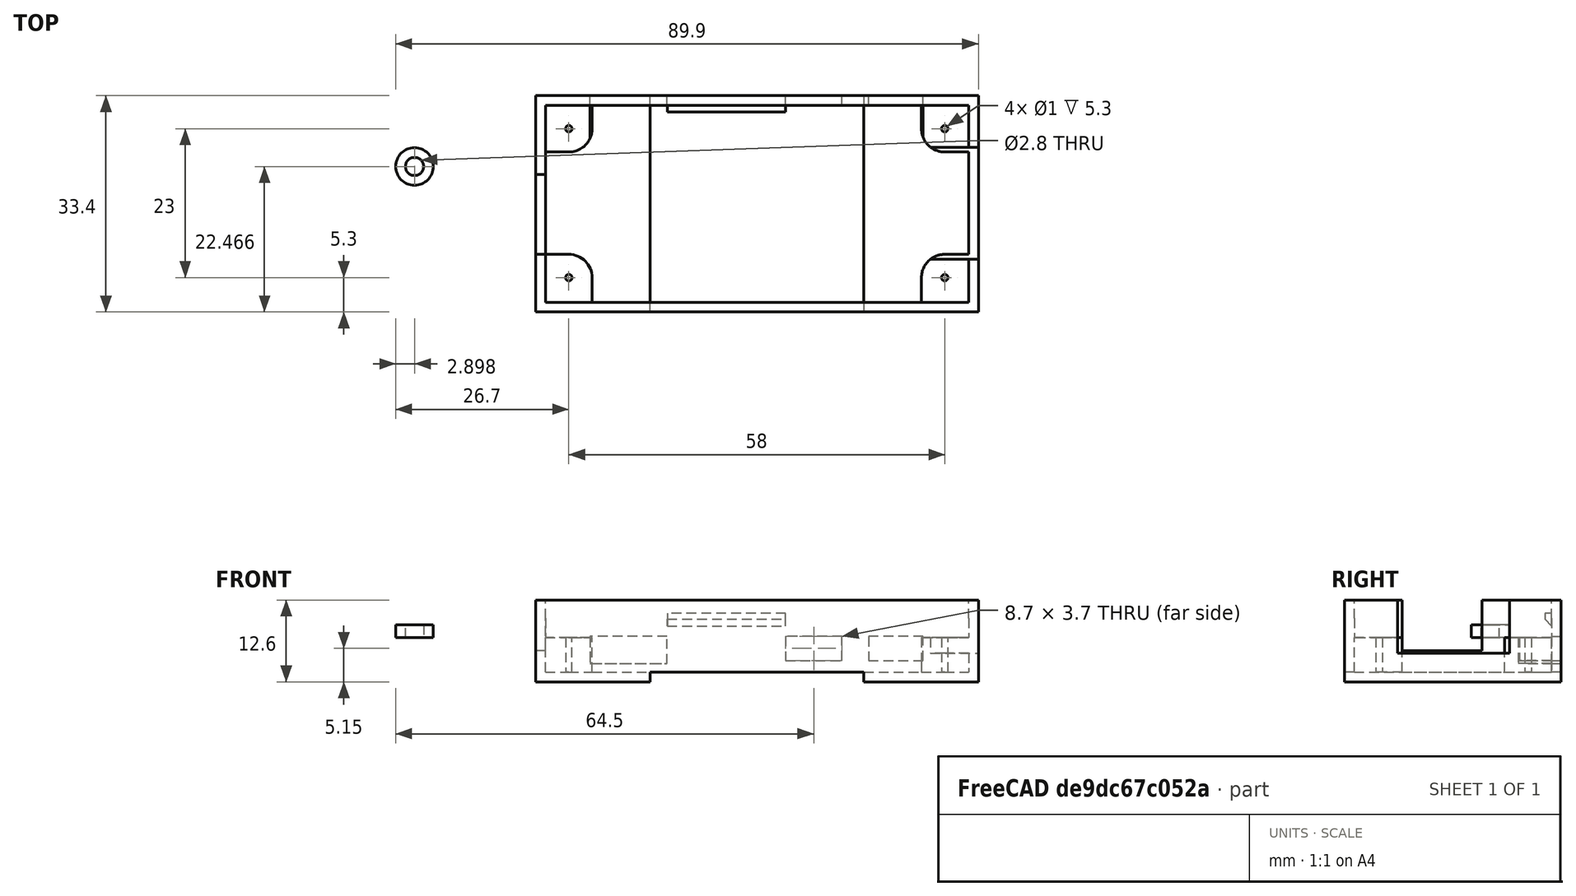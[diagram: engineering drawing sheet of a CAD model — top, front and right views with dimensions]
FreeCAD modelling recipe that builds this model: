
FCSTD DOCUMENT  (FreeCAD 0.18.3R)
Label: PI.Capsule
License: All rights reserved
LicenseURL: http://en.wikipedia.org/wiki/All_rights_reserved
objects: Part::Part2DObjectPython×32, Part::Extrusion×32, Part::Cut×15, Part::MultiFuse×7
note: 86 computed .brp shape members not serialized (recipe doc carries the construction recipe); baked Part::Feature solids carry a one-line shape summary decoded from their .brp

FEATURE [Part::Part2DObjectPython] Rectangle  # Draft 2D object (typed FeaturePython)
  ChamferSize = 0
  Columns = 1
  FilletRadius = 0
  Height = 33.4
  Length = 68.3
  MakeFace = true
  Placement = pos=(0,0,0) rot=(1,0,0;3.14159rad)
  Rows = 1
FEATURE [Part::Part2DObjectPython] Rectangle001  # Draft 2D object (typed FeaturePython)
  ChamferSize = 0
  Columns = 1
  FilletRadius = 0
  Height = 30.4
  Length = 65.3
  MakeFace = true
  Placement = pos=(1.5,-1.5,0) rot=(1,0,0;3.14159rad)
  Rows = 1
FEATURE [Part::Part2DObjectPython] Circle004  # Draft 2D object (typed FeaturePython)
  FirstAngle = 0
  LastAngle = 0
  MakeFace = true
  Placement = pos=(5.1,-5.1,-8.3) rot=(0,0,-1;1.5708rad)
  Radius = 3.6
FEATURE [Part::Part2DObjectPython] Circle006  # Draft 2D object (typed FeaturePython)
  FirstAngle = 0
  LastAngle = 0
  MakeFace = true
  Placement = pos=(63.1,-5.1,-8.3) rot=(0,0,1;0rad)
  Radius = 3.6
FEATURE [Part::Part2DObjectPython] Rectangle006  # Draft 2D object (typed FeaturePython)
  ChamferSize = 0
  Columns = 1
  FilletRadius = 0
  Height = 4.1
  Length = 11.9
  MakeFace = true
  Placement = pos=(8.375,-1.5,-7) rot=(1,0,0;1.5708rad)
  Rows = 1
FEATURE [Part::Part2DObjectPython] Rectangle007  # Draft 2D object (typed FeaturePython)
  ChamferSize = 0
  Columns = 1
  FilletRadius = 0
  Height = 3.7
  Length = 8.7
  MakeFace = true
  Placement = pos=(38.55,-1.5,-6.5) rot=(1,0,0;1.5708rad)
  Rows = 1
FEATURE [Part::Part2DObjectPython] Rectangle008  # Draft 2D object (typed FeaturePython)
  ChamferSize = 0
  Columns = 1
  FilletRadius = 0
  Height = 3.7
  Length = 8.4
  MakeFace = true
  Placement = pos=(51.35,-1.5,-6.5) rot=(1,0,0;1.5708rad)
  Rows = 1
  Support = -> [Rectangle007]
FEATURE [Part::Extrusion] Extrude020
  Base = -> Circle006
  Dir = (0,0,1)
  DirMode = 2
  FaceMakerClass = Part::FaceMakerBullseye
  LengthFwd = 5.3
  LengthRev = 0
  Solid = false
  Symmetric = false
FEATURE [Part::Extrusion] Extrude021
  Base = -> Circle004
  Dir = (0,0,1)
  DirMode = 2
  FaceMakerClass = Part::FaceMakerBullseye
  LengthFwd = 5.3
  LengthRev = 0
  Solid = false
  Symmetric = false
FEATURE [Part::Part2DObjectPython] Rectangle013  # Draft 2D object (typed FeaturePython)
  ChamferSize = 0
  Columns = 1
  FilletRadius = 0
  Height = 7.2
  Length = 3.6
  MakeFace = true
  Placement = pos=(1.5,-8.7,-8.3) rot=(0,0,1;0rad)
  Rows = 1
  Support = -> [Rectangle]
FEATURE [Part::Part2DObjectPython] Rectangle014  # Draft 2D object (typed FeaturePython)
  ChamferSize = 0
  Columns = 1
  FilletRadius = 0
  Height = 3.6
  Length = 7.2
  MakeFace = true
  Placement = pos=(1.5,-5.1,-8.3) rot=(0,0,1;0rad)
  Rows = 1
FEATURE [Part::Part2DObjectPython] Circle008  # Draft 2D object (typed FeaturePython)
  FirstAngle = 0
  LastAngle = 0
  MakeFace = true
  Placement = pos=(63.1,-5.1,-8.3) rot=(0,0,1;0rad)
  Radius = 0.5
FEATURE [Part::Extrusion] Extrude027
  Base = -> Circle008
  Dir = (0,0,1)
  DirMode = 2
  FaceMakerClass = Part::FaceMakerBullseye
  LengthFwd = 5.3
  LengthRev = 0
  Solid = false
  Symmetric = false
FEATURE [Part::Extrusion] Extrude028
  Base = -> Rectangle013
  Dir = (0,0,1)
  DirMode = 2
  FaceMakerClass = Part::FaceMakerBullseye
  LengthFwd = 5.3
  LengthRev = 0
  Solid = false
  Symmetric = false
FEATURE [Part::Extrusion] Extrude029
  Base = -> Rectangle014
  Dir = (0,0,1)
  DirMode = 2
  FaceMakerClass = Part::FaceMakerBullseye
  LengthFwd = 5.3
  LengthRev = 0
  Solid = false
  Symmetric = false
FEATURE [Part::MultiFuse] Fusion002
  Shapes = -> [Extrude028,Extrude029,Extrude021]
FEATURE [Part::Part2DObjectPython] Circle009  # Draft 2D object (typed FeaturePython)
  FirstAngle = 0
  LastAngle = 0
  MakeFace = true
  Placement = pos=(5.1,-5.1,-8.3) rot=(0,0,1;0rad)
  Radius = 0.5
FEATURE [Part::Extrusion] Extrude030
  Base = -> Circle009
  Dir = (0,0,1)
  DirMode = 2
  FaceMakerClass = Part::FaceMakerBullseye
  LengthFwd = 5.3
  LengthRev = 0
  Solid = false
  Symmetric = false
FEATURE [Part::Cut] Cut002
  Base = -> Fusion002
  Tool = -> Extrude030
FEATURE [Part::Part2DObjectPython] Circle010  # Draft 2D object (typed FeaturePython)
  FirstAngle = 0
  LastAngle = 0
  MakeFace = true
  Placement = pos=(5.1,-28.1,-8.3) rot=(1,0,0;3.14159rad)
  Radius = 0.5
FEATURE [Part::Extrusion] Extrude033
  Base = -> Circle010
  Dir = (0,0,-1)
  DirMode = 2
  FaceMakerClass = Part::FaceMakerBullseye
  LengthFwd = -5.3
  LengthRev = 0
  Solid = false
  Symmetric = false
FEATURE [Part::Part2DObjectPython] Circle011  # Draft 2D object (typed FeaturePython)
  FirstAngle = 0
  LastAngle = 0
  MakeFace = true
  Placement = pos=(5.1,-28.1,-8.3) rot=(1,0,0;3.14159rad)
  Radius = 3.6
FEATURE [Part::Part2DObjectPython] Rectangle019  # Draft 2D object (typed FeaturePython)
  ChamferSize = 0
  Columns = 1
  FilletRadius = 0
  Height = 3.8
  Length = 7.2
  MakeFace = true
  Placement = pos=(1.5,-31.9,-8.3) rot=(0,0,1;0rad)
  Rows = 1
FEATURE [Part::Part2DObjectPython] Rectangle020  # Draft 2D object (typed FeaturePython)
  ChamferSize = 0
  Columns = 1
  FilletRadius = 0
  Height = 7.4
  Length = 3.6
  MakeFace = true
  Placement = pos=(1.5,-31.9,-8.3) rot=(0,0,1;0rad)
  Rows = 1
FEATURE [Part::Extrusion] Extrude
  Base = -> Circle011
  Dir = (0,0,-1)
  DirMode = 2
  FaceMakerClass = Part::FaceMakerBullseye
  LengthFwd = -5.3
  LengthRev = 0
  Solid = false
  Symmetric = false
FEATURE [Part::Extrusion] Extrude034
  Base = -> Rectangle019
  Dir = (0,0,1)
  DirMode = 2
  FaceMakerClass = Part::FaceMakerBullseye
  LengthFwd = 5.3
  LengthRev = 0
  Solid = false
  Symmetric = false
FEATURE [Part::Extrusion] Extrude035
  Base = -> Rectangle020
  Dir = (0,0,1)
  DirMode = 2
  FaceMakerClass = Part::FaceMakerBullseye
  LengthFwd = 5.3
  LengthRev = 0
  Solid = false
  Symmetric = false
FEATURE [Part::MultiFuse] Fusion003
  Shapes = -> [Extrude034,Extrude035,Extrude]
FEATURE [Part::Cut] Cut003
  Base = -> Fusion003
  Tool = -> Extrude033
FEATURE [Part::Extrusion] Extrude036
  Base = -> Rectangle001
  Dir = (0,0,-1)
  DirMode = 2
  FaceMakerClass = Part::FaceMakerBullseye
  LengthFwd = 8.3
  LengthRev = 0
  Solid = false
  Symmetric = false
FEATURE [Part::Extrusion] Extrude037
  Base = -> Rectangle
  Dir = (0,0,-1)
  DirMode = 2
  FaceMakerClass = Part::FaceMakerBullseye
  LengthFwd = 9.8
  LengthRev = 0
  Solid = false
  Symmetric = false
FEATURE [Part::Part2DObjectPython] Circle012  # Draft 2D object (typed FeaturePython)
  FirstAngle = 0
  LastAngle = 0
  MakeFace = true
  Placement = pos=(63.1,-28.1,-3) rot=(0,0,1;0rad)
  Radius = 3.6
FEATURE [Part::Part2DObjectPython] Circle013  # Draft 2D object (typed FeaturePython)
  FirstAngle = 0
  LastAngle = 0
  MakeFace = true
  Placement = pos=(63.1,-28.1,-3) rot=(0,0,1;0rad)
  Radius = 0.5
FEATURE [Part::Part2DObjectPython] Rectangle021  # Draft 2D object (typed FeaturePython)
  ChamferSize = 0
  Columns = 1
  FilletRadius = 0
  Height = 7.4
  Length = 3.7
  MakeFace = true
  Placement = pos=(63.1,-31.9,-3) rot=(0,0,1;0rad)
  Rows = 1
FEATURE [Part::Part2DObjectPython] Rectangle022  # Draft 2D object (typed FeaturePython)
  ChamferSize = 0
  Columns = 1
  FilletRadius = 0
  Height = 3.8
  Length = 7.3
  MakeFace = true
  Placement = pos=(59.5,-31.9,-3) rot=(0,0,1;0rad)
  Rows = 1
FEATURE [Part::Extrusion] Extrude038
  Base = -> Rectangle021
  Dir = (0,0,1)
  DirMode = 2
  FaceMakerClass = Part::FaceMakerBullseye
  LengthFwd = -5.3
  LengthRev = 0
  Solid = false
  Symmetric = false
FEATURE [Part::Extrusion] Extrude039
  Base = -> Rectangle022
  Dir = (0,0,1)
  DirMode = 2
  FaceMakerClass = Part::FaceMakerBullseye
  LengthFwd = -5.3
  LengthRev = 0
  Solid = false
  Symmetric = false
FEATURE [Part::Extrusion] Extrude040
  Base = -> Circle012
  Dir = (0,0,1)
  DirMode = 2
  FaceMakerClass = Part::FaceMakerBullseye
  LengthFwd = -5.3
  LengthRev = 0
  Solid = false
  Symmetric = false
FEATURE [Part::MultiFuse] Fusion
  Shapes = -> [Extrude038,Extrude039,Extrude040]
FEATURE [Part::Extrusion] Extrude041
  Base = -> Circle013
  Dir = (0,0,1)
  DirMode = 2
  FaceMakerClass = Part::FaceMakerBullseye
  LengthFwd = -5.3
  LengthRev = 0
  Solid = false
  Symmetric = false
FEATURE [Part::Cut] Cut
  Base = -> Fusion
  Tool = -> Extrude041
FEATURE [Part::Part2DObjectPython] Rectangle024  # Draft 2D object (typed FeaturePython)
  ChamferSize = 0
  Columns = 1
  FilletRadius = 0
  Height = 3.6
  Length = 7.3
  MakeFace = true
  Placement = pos=(59.5,-5.1,-3) rot=(0,0,1;0rad)
  Rows = 1
FEATURE [Part::Part2DObjectPython] Rectangle025  # Draft 2D object (typed FeaturePython)
  ChamferSize = 0
  Columns = 1
  FilletRadius = 0
  Height = 7.19976
  Length = 3.7019
  MakeFace = true
  Placement = pos=(63.1,-8.7,-3) rot=(0,0,1;0rad)
  Rows = 1
FEATURE [Part::Extrusion] Extrude042
  Base = -> Rectangle025
  Dir = (0,0,1)
  DirMode = 2
  FaceMakerClass = Part::FaceMakerBullseye
  LengthFwd = -5.3
  LengthRev = 0
  Solid = false
  Symmetric = false
FEATURE [Part::Extrusion] Extrude043
  Base = -> Rectangle024
  Dir = (0,0,1)
  DirMode = 2
  FaceMakerClass = Part::FaceMakerBullseye
  LengthFwd = -5.3
  LengthRev = 0
  Solid = false
  Symmetric = false
FEATURE [Part::MultiFuse] Fusion004
  Shapes = -> [Extrude043,Extrude042,Extrude020]
FEATURE [Part::Cut] Cut005
  Base = -> Fusion004
  Tool = -> Extrude027
FEATURE [Part::MultiFuse] Fusion013
  Shapes = -> [Cut005,Cut]
FEATURE [Part::Extrusion] Extrude046
  Base = -> Rectangle006
  Dir = (0,-1,2e-16)
  DirMode = 2
  FaceMakerClass = Part::FaceMakerBullseye
  LengthFwd = 7
  LengthRev = 0
  Solid = false
  Symmetric = false
FEATURE [Part::Cut] Cut008
  Base = -> Cut002
  Tool = -> Extrude046
FEATURE [Part::Part2DObjectPython] Rectangle028  # Draft 2D object (typed FeaturePython)
  ChamferSize = 0
  Columns = 1
  FilletRadius = 0
  Height = 4.2
  Length = 11.9
  MakeFace = true
  Placement = pos=(8.375,-1.5,-7) rot=(1,0,0;1.5708rad)
  Rows = 1
FEATURE [Part::Part2DObjectPython] Rectangle029  # Draft 2D object (typed FeaturePython)
  ChamferSize = 0
  Columns = 1
  FilletRadius = 0
  Height = 3.6
  Length = 8.4
  MakeFace = true
  Placement = pos=(51.35,-1.5,-6.5) rot=(1,0,0;1.5708rad)
  Rows = 1
FEATURE [Part::Extrusion] Extrude050
  Base = -> Rectangle029
  Dir = (0,-1,2e-16)
  DirMode = 2
  FaceMakerClass = Part::FaceMakerBullseye
  LengthFwd = 7
  LengthRev = 0
  Placement = pos=(7.1e-15,-9e-16,0) rot=(0,0,1;0rad)
  Solid = false
  Symmetric = false
FEATURE [Part::Part2DObjectPython] Rectangle048  # Draft 2D object (typed FeaturePython)
  ChamferSize = 0
  Columns = 1
  FilletRadius = 0
  Height = 4.99807
  Length = 12.3
  MakeFace = true
  Placement = pos=(1.5,-24.5,-4.99807) rot=(0.57735,0.57735,0.57735;2.0944rad)
  Rows = 1
FEATURE [Part::Extrusion] Extrude096
  Base = -> Rectangle048
  Dir = (1,0,0)
  DirMode = 2
  FaceMakerClass = Part::FaceMakerBullseye
  LengthFwd = -1.5
  LengthRev = 0
  Solid = false
  Symmetric = false
FEATURE [Part::Part2DObjectPython] Rectangle071  # Draft 2D object (typed FeaturePython)
  ChamferSize = 0
  Columns = 1
  FilletRadius = 0
  Height = 33.4
  Length = 32.95
  MakeFace = true
  Placement = pos=(17.675,2e-15,-9.8) rot=(1,0,0;3.14159rad)
  Rows = 1
FEATURE [Part::Extrusion] Extrude168
  Base = -> Rectangle071
  Dir = (0,0,-1)
  DirMode = 2
  FaceMakerClass = Part::FaceMakerBullseye
  LengthFwd = -1.5
  LengthRev = 0
  Solid = false
  Symmetric = false
FEATURE [Part::Cut] Cut004
  Base = -> Extrude037
  Tool = -> Extrude036
FEATURE [Part::Part2DObjectPython] Rectangle027  # Draft 2D object (typed FeaturePython)
  ChamferSize = 0
  Columns = 1
  FilletRadius = 0
  Height = 5.4
  Length = 17.3
  MakeFace = true
  Placement = pos=(60.9006,-7.95,-5.4) rot=(0.57735,-0.57735,-0.57735;2.0944rad)
  Rows = 1
  Support = -> [Cut004]
FEATURE [Part::Extrusion] Extrude081
  Base = -> Rectangle027
  Dir = (-1,0,0)
  DirMode = 2
  FaceMakerClass = Part::FaceMakerBullseye
  LengthFwd = -8
  LengthRev = 0
  Solid = false
  Symmetric = false
FEATURE [Part::Extrusion] Extrude169
  Base = -> Rectangle028
  Dir = (0,-1,2e-16)
  DirMode = 2
  FaceMakerClass = Part::FaceMakerBullseye
  LengthFwd = -1.5
  LengthRev = 0
  Solid = false
  Symmetric = false
FEATURE [Part::Extrusion] Extrude170
  Base = -> Rectangle007
  Dir = (0,-1,2e-16)
  DirMode = 2
  FaceMakerClass = Part::FaceMakerBullseye
  LengthFwd = -1.5
  LengthRev = 0
  Solid = false
  Symmetric = false
FEATURE [Part::Extrusion] Extrude171
  Base = -> Rectangle008
  Dir = (0,-1,2e-16)
  DirMode = 2
  FaceMakerClass = Part::FaceMakerBullseye
  LengthFwd = -1.5
  LengthRev = 0
  Solid = false
  Symmetric = false
FEATURE [Part::MultiFuse] Fusion034
  Shapes = -> [Cut003,Cut008,Fusion013,Cut004]
FEATURE [Part::Cut] Cut079
  Base = -> Fusion034
  Tool = -> Extrude081
FEATURE [Part::Cut] Cut080
  Base = -> Cut079
  Tool = -> Extrude096
FEATURE [Part::Cut] Cut081
  Base = -> Cut080
  Tool = -> Extrude169
FEATURE [Part::Cut] Cut082
  Base = -> Cut081
  Tool = -> Extrude170
FEATURE [Part::Cut] Cut083
  Base = -> Cut082
  Tool = -> Extrude171
FEATURE [Part::Cut] Cut084
  Base = -> Cut083
  Tool = -> Extrude050
FEATURE [Part::Cut] Cut085
  Base = -> Cut084
  Tool = -> Extrude168
FEATURE [Part::Part2DObjectPython] Wire  # Draft 2D object (typed FeaturePython)
  ChamferSize = 0
  Closed = true
  End = (0,0,0)
  FilletRadius = 0
  Length = 173.9
  MakeFace = true
  Placement = pos=(1.4e-14,-12.2,0) rot=(1,0,0;1.5708rad)
  Points = (8) [(0,0,0),(1.5,-4.59243e-17,0),(1.5,2.32995e-15,-10.7),(66.8,3.30717e-16,-10.7),(66.8,-1.98965e-15,-4.25),(68.3,-2.03557e-15,-4.25),+2 more]
  Start = (1.4e-14,-12.2,0)
  Subdivisions = 0
FEATURE [Part::Extrusion] Extrusion
  Base = -> Wire
  Dir = (0,0,2.8)
  DirMode = 0
  FaceMakerClass = Part::FaceMakerBullseye
  LengthFwd = 0
  LengthRev = 0
  Solid = true
  Symmetric = false
FEATURE [Part::Part2DObjectPython] Wire004  # Draft 2D object (typed FeaturePython)
  ChamferSize = 0
  Closed = true
  End = (0,-33.4,0)
  FilletRadius = 0
  Length = 167.7
  MakeFace = true
  Placement = pos=(1.4e-14,-24.5,0) rot=(0,0,1;0rad)
  Points = (8) [(0,0,0),(1.5,0,0),(1.5,-7.4,0),(66.8,-7.4,0),(66.8,-0.75,-8.88178e-16),(68.3,-0.75,-8.88178e-16),(68.3,-8.9,0),(-1.42613e-14,-8.9,0)]
  Start = (1.4e-14,-24.5,0)
  Subdivisions = 0
FEATURE [Part::Extrusion] Extrusion001
  Base = -> Wire004
  Dir = (0,0,2.8)
  DirMode = 0
  FaceMakerClass = Part::FaceMakerBullseye
  LengthFwd = 0
  LengthRev = 0
  Solid = true
  Symmetric = false
FEATURE [Part::Part2DObjectPython] Rectangle072  # Draft 2D object (typed FeaturePython)
  ChamferSize = 0
  Columns = 1
  FilletRadius = 0
  Height = 2
  Length = 18.2517
  MakeFace = true
  Placement = pos=(20.2983,-1.5,-1.2) rot=(1,0,0;1.5708rad)
  Rows = 1
FEATURE [Part::Extrusion] Extrude172
  Base = -> Rectangle072
  Dir = (0,-1,2e-16)
  DirMode = 2
  FaceMakerClass = Part::FaceMakerBullseye
  LengthFwd = 1
  LengthRev = 0
  Solid = false
  Symmetric = false
FEATURE [Part::Part2DObjectPython] Wire005  # Draft 2D object (typed FeaturePython)
  ChamferSize = 0
  Closed = true
  End = (20.2983,-2.5,-1.2)
  FilletRadius = 0
  Length = 3.5312
  MakeFace = true
  Placement = pos=(20.2983,-1.5,-1.2) rot=(0.57735,-0.57735,-0.57735;2.0944rad)
  Points = (3) [(0,0,0),(1,1.06806,0),(1,2.22045e-16,0)]
  Start = (20.2983,-1.5,-1.2)
  Subdivisions = 0
  Support = -> [Extrude172]
FEATURE [Part::Extrusion] Extrude173
  Base = -> Wire005
  Dir = (-1,1e-16,-1e-16)
  DirMode = 2
  FaceMakerClass = Part::FaceMakerBullseye
  LengthFwd = -20
  LengthRev = 0
  Solid = false
  Symmetric = false
FEATURE [Part::Cut] Cut086
  Base = -> Extrude172
  Tool = -> Extrude173
FEATURE [Part::MultiFuse] Fusion035
  Shapes = -> [Cut085,Extrusion,Extrusion001,Cut086]
FEATURE [Part::Part2DObjectPython] Circle  # Draft 2D object (typed FeaturePython)
  FirstAngle = 0
  LastAngle = 0
  MakeFace = true
  Placement = pos=(-18.7021,-10.934,-3) rot=(0,0,1;0rad)
  Radius = 2.9
FEATURE [Part::Extrusion] Extrude174
  Base = -> Circle
  Dir = (0,0,1)
  DirMode = 2
  FaceMakerClass = Part::FaceMakerBullseye
  LengthFwd = 2
  LengthRev = 0
  Solid = false
  Symmetric = false
FEATURE [Part::Part2DObjectPython] Circle014  # Draft 2D object (typed FeaturePython)
  FirstAngle = 0
  LastAngle = 0
  MakeFace = true
  Placement = pos=(-18.7021,-10.934,-1) rot=(0,0,1;0rad)
  Radius = 1.4
FEATURE [Part::Extrusion] Extrude175
  Base = -> Circle014
  Dir = (0,0,1)
  DirMode = 2
  FaceMakerClass = Part::FaceMakerBullseye
  LengthFwd = -2
  LengthRev = 0
  Solid = false
  Symmetric = false
FEATURE [Part::Cut] Cut087
  Base = -> Extrude174
  Tool = -> Extrude175
